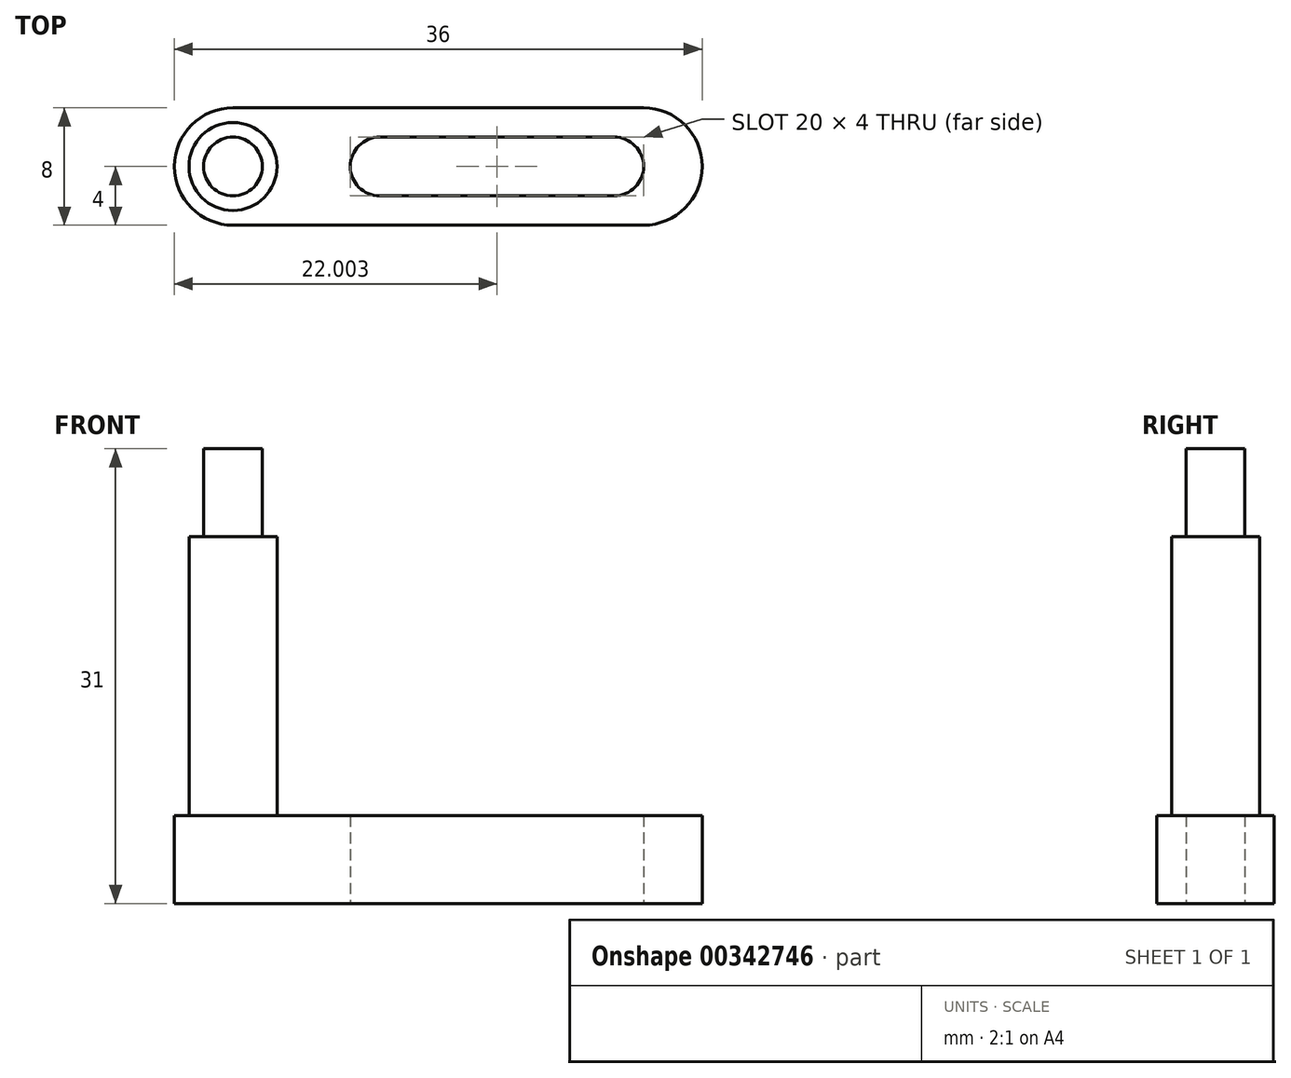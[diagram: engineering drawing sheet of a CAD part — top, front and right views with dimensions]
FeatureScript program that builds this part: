
annotation { "Feature Type Name" : "Feature", "Feature Type Description" : "" }
export const myFeature = defineFeature(function(context is Context, id is Id, definition is map)
    precondition{}
    {
        {
            var Q0;
            Q0=qCreatedBy(makeId("Top.planeOp"),FACE);
            var sketch = newSketch(context, id + "F0", { "sketchPlane" : qUnion([Q0])});
            skLineSegment(sketch, "E0", {"start": v(-56.74, 4) * mm, "end": v(-28.74, 4) * mm});
            skArc(sketch, "E1", {"start": v(-28.74, 4) * mm, "mid": v(-25.9, 2.83) * mm, "end": v(-24.74, 0) * mm});
            skLineSegment(sketch, "E2", {"start": v(-46.74, 2) * mm, "end": v(-30.74, 2) * mm});
            skArc(sketch, "E3", {"start": v(-48.74, 0) * mm, "mid": v(-48.15, 1.41) * mm, "end": v(-46.74, 2) * mm});
            skArc(sketch, "E4", {"start": v(-28.74, 0) * mm, "mid": v(-29.32, 1.41) * mm, "end": v(-30.74, 2) * mm});
            skArc(sketch, "E5", {"start": v(-56.74, 4) * mm, "mid": v(-59.57, 2.83) * mm, "end": v(-60.74, 0) * mm});
            skArc(sketch, "E6.MirrorCS", {"start": v(-56.74, -4) * mm, "mid": v(-59.57, -2.83) * mm, "end": v(-60.74, 0) * mm});
            skLineSegment(sketch, "E7.MirrorCS", {"start": v(-56.74, -4) * mm, "end": v(-28.74, -4) * mm});
            skArc(sketch, "E8.MirrorCS", {"start": v(-28.74, -4) * mm, "mid": v(-25.9, -2.83) * mm, "end": v(-24.74, 0) * mm});
            skArc(sketch, "E9.MirrorCS", {"start": v(-28.74, 0) * mm, "mid": v(-29.32, -1.41) * mm, "end": v(-30.74, -2) * mm});
            skLineSegment(sketch, "E10.MirrorCS", {"start": v(-46.74, -2) * mm, "end": v(-30.74, -2) * mm});
            skArc(sketch, "E11.MirrorCS", {"start": v(-48.74, 0) * mm, "mid": v(-48.15, -1.41) * mm, "end": v(-46.74, -2) * mm});
            skSolve(sketch);
        }
        {
            var Q0;
            Q0=makeQuery(id+"F0.imprint","IMPRINT",FACE,{"disambiguationData":[TD([[makeQuery(id+"F0.imprint","IMPRINT",EDGE,{"derivedFrom":sQuery(id+"F0.wireOp",EDGE,"E0")}),-1.0]])]});
            extrude(context, id + "F1", {"entities" : qUnion([Q0]), "depth" : 6 * mm});
        }
        {
            var Q0;
            Q0=makeQuery(id+"F1.opExtrude","CAP_FACE",FACE,{"disambiguationData":[OSD([sQuery(id+"F0.wireOp",EDGE,"E0"),sQuery(id+"F0.wireOp",EDGE,"E1"),sQuery(id+"F0.wireOp",EDGE,"E2"),sQuery(id+"F0.wireOp",EDGE,"E3"),sQuery(id+"F0.wireOp",EDGE,"E4"),sQuery(id+"F0.wireOp",EDGE,"E5"),sQuery(id+"F0.wireOp",EDGE,"E6.MirrorCS"),sQuery(id+"F0.wireOp",EDGE,"E7.MirrorCS"),sQuery(id+"F0.wireOp",EDGE,"E8.MirrorCS"),sQuery(id+"F0.wireOp",EDGE,"E9.MirrorCS"),sQuery(id+"F0.wireOp",EDGE,"E10.MirrorCS"),sQuery(id+"F0.wireOp",EDGE,"E11.MirrorCS")])],"isStart":false});
            var sketch = newSketch(context, id + "F2", { "sketchPlane" : qUnion([Q0])});
            skCircle(sketch, "E12", {"center": v(-56.74, 0) * mm, "radius": 3 * mm});
            skSolve(sketch);
        }
        {
            var Q0;
            Q0=makeQuery(id+"F2.imprint","IMPRINT",FACE,{"disambiguationData":[TD([[makeQuery(id+"F2.imprint","IMPRINT",EDGE,{"derivedFrom":sQuery(id+"F2.wireOp",EDGE,"E12")}),1.0]])]});
            extrude(context, id + "F3", {"entities" : qUnion([Q0]), "operationType" : NewBodyOperationType.ADD, "depth" : 19 * mm});
        }
        {
            var Q0;
            Q0=makeQuery(id+"F3.opExtrude","CAP_FACE",FACE,{"disambiguationData":[OSD([sQuery(id+"F2.wireOp",EDGE,"E12")])],"isStart":false});
            var sketch = newSketch(context, id + "F4", { "sketchPlane" : qUnion([Q0])});
            skCircle(sketch, "E13", {"center": v(-56.74, 0) * mm, "radius": 2 * mm});
            skSolve(sketch);
        }
        {
            var Q0;
            Q0=makeQuery(id+"F4.imprint","IMPRINT",FACE,{"disambiguationData":[TD([[makeQuery(id+"F4.imprint","IMPRINT",EDGE,{"derivedFrom":sQuery(id+"F4.wireOp",EDGE,"E13")}),1.0]])]});
            extrude(context, id + "F5", {"entities" : qUnion([Q0]), "operationType" : NewBodyOperationType.ADD, "depth" : 6 * mm});
        }
    });
